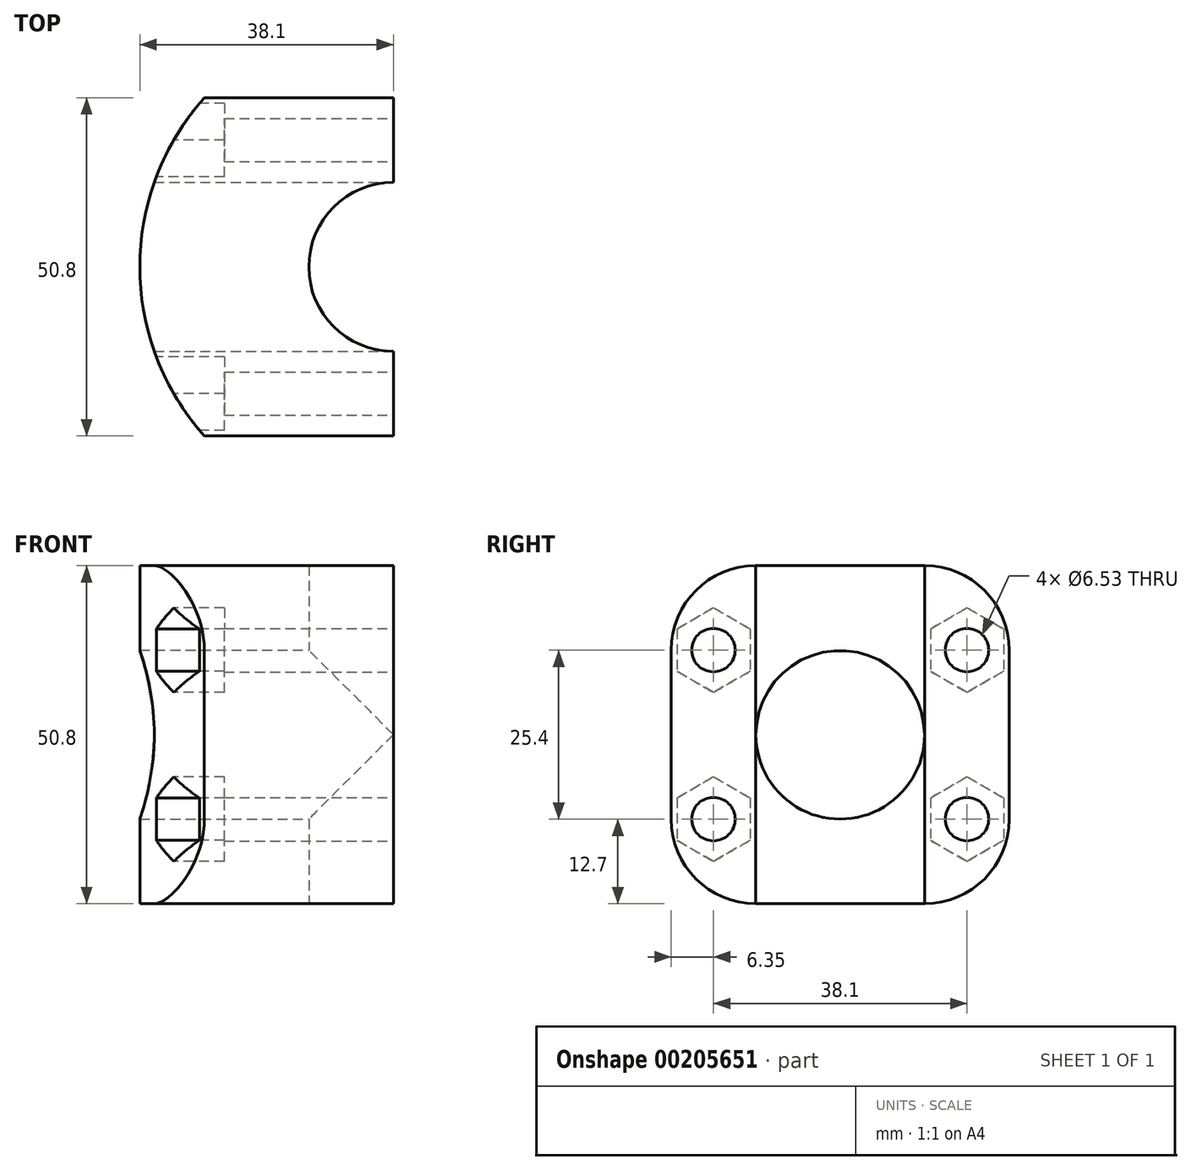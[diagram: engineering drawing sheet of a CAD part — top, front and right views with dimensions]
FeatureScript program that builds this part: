
annotation { "Feature Type Name" : "Feature", "Feature Type Description" : "" }
export const myFeature = defineFeature(function(context is Context, id is Id, definition is map)
    precondition{}
    {
        {
            var Q0;
            Q0=qCreatedBy(makeId("Top.planeOp"),FACE);
            var sketch = newSketch(context, id + "F0", { "sketchPlane" : qUnion([Q0])});
            skLineSegment(sketch, "E0.bottom", {"start": v(-28.4, 50.8) * mm, "end": v(0, 50.8) * mm});
            skLineSegment(sketch, "E0.top", {"start": v(-28.4, 0) * mm, "end": v(0, 0) * mm});
            skLineSegment(sketch, "E0.right", {"start": v(0, 50.8) * mm, "end": v(0, 38.1) * mm});
            skArc(sketch, "E1", {"start": v(0, 38.1) * mm, "mid": v(-12.7, 25.4) * mm, "end": v(0, 12.7) * mm});
            skArc(sketch, "E2", {"start": v(-28.4, 50.8) * mm, "mid": v(-38.1, 25.4) * mm, "end": v(-28.4, 0) * mm});
            skLineSegment(sketch, "E3.trimOffspring", {"start": v(0, 12.7) * mm, "end": v(0, 0) * mm});
            skSolve(sketch);
        }
        {
            var Q0;
            Q0 = qSketchRegion(id + "F0", true);
            extrude(context, id + "F1", {"entities" : qUnion([Q0]), "endBound" : BoundingType.SYMMETRIC, "depth" : 50.8 * mm});
        }
        {
            var Q0;
            Q0=qCreatedBy(makeId("Right.planeOp"),FACE);
            var sketch = newSketch(context, id + "F2", { "sketchPlane" : qUnion([Q0])});
            skPoint(sketch, "E4", {"position": v(44.45, 12.7) * mm});
            skPoint(sketch, "E5", {"position": v(44.45, -12.7) * mm});
            skPoint(sketch, "E6", {"position": v(6.35, -12.7) * mm});
            skPoint(sketch, "E7", {"position": v(6.35, 12.7) * mm});
            skLineSegment(sketch, "E8", {"start": v(50.8, 12.7) * mm, "end": v(0, 12.7) * mm});
            skLineSegment(sketch, "E9", {"start": v(50.8, -12.7) * mm, "end": v(0, -12.7) * mm});
            skLineSegment(sketch, "E10", {"start": v(6.35, 25.4) * mm, "end": v(6.35, -25.4) * mm});
            skLineSegment(sketch, "E11", {"start": v(44.45, 25.4) * mm, "end": v(44.45, -25.4) * mm});
            skLineSegment(sketch, "E12", {"start": v(25.4, 12.7) * mm, "end": v(25.4, -12.7) * mm});
            skLineSegment(sketch, "E13", {"start": v(6.35, 0) * mm, "end": v(44.45, 0) * mm});
            skPoint(sketch, "E14", {"position": v(25.4, 0) * mm});
            skSolve(sketch);
        }
        {
            var Q0;
            Q0=sQuery(id+"F2.wireOp",VERTEX,"E7");
            var Q1;
            Q1=sQuery(id+"F2.wireOp",VERTEX,"E4");
            var Q2;
            Q2=sQuery(id+"F2.wireOp",VERTEX,"E5");
            var Q3;
            Q3=sQuery(id+"F2.wireOp",VERTEX,"E6");
            var Q4;
            Q4=makeQuery(id+"F1.opExtrude","SWEPT_BODY",BODY,{"disambiguationData":[OSD([sQuery(id+"F0.wireOp",EDGE,"E0.bottom"),sQuery(id+"F0.wireOp",EDGE,"E0.top"),sQuery(id+"F0.wireOp",EDGE,"E0.right"),sQuery(id+"F0.wireOp",EDGE,"E1"),sQuery(id+"F0.wireOp",EDGE,"E2"),sQuery(id+"F0.wireOp",EDGE,"E3.trimOffspring")])]});
            hole(context, id + "F3", {"style" : HoleStyle.SIMPLE, "endStyle" : HoleEndStyle.THROUGH, "standardTappedOrClearance" : lookupTablePath({ "standard" : "ANSI", "fit" : "Close", "size" : "1/4", "type" : "Clearance" }), "standardBlindInLast" : lookupTablePath({ "fit" : "Close", "standard" : "ANSI", "size" : "1/4", "type" : "Clearance" }), "holeDiameter" : 6.53 * mm, "locations" : qUnion([Q0, Q1, Q2, Q3]), "scope" : qUnion([Q4]), "isTappedThrough" : true});
        }
        {
            var Q0;
            Q0=makeQuery(id+"F1.opExtrude","CAP_EDGE",EDGE,{"disambiguationData":[OSD([sQuery(id+"F0.wireOp",EDGE,"E2")])],"isStart":false});
            cPoint(context, id + "F4", {"entities" : qUnion([Q0]), "parameter" : 0.5});
        }
        {
            var Q0;
            Q0=qCreatedBy(makeId("Right.planeOp"),FACE);
            var Q1;
            Q1 = qCreatedBy(id + "F4" ,VERTEX);
            cPlane(context, id + "F5", {"entities" : qUnion([Q0, Q1]), "cplaneType" : CPlaneType.PLANE_POINT, "offset" : 25.4 * mm, "width" : 152.4 * mm, "height" : 152.4 * mm});
        }
        {
            var Q0;
            Q0=qCreatedBy(id+"F5.planeOp",FACE);
            var sketch = newSketch(context, id + "F6", { "sketchPlane" : qUnion([Q0])});
            skCircle(sketch, "E15.cCircle", {"center": v(6.35, 12.7) * mm, "radius": 5.5 * mm, "construction": true});
            skLineSegment(sketch, "E15.0", {"start": v(0.85, 9.52) * mm, "end": v(0.85, 15.88) * mm});
            skLineSegment(sketch, "E15.1", {"start": v(0.85, 15.88) * mm, "end": v(6.35, 19.05) * mm});
            skLineSegment(sketch, "E15.2", {"start": v(6.35, 19.05) * mm, "end": v(11.85, 15.88) * mm});
            skLineSegment(sketch, "E15.3", {"start": v(11.85, 15.88) * mm, "end": v(11.85, 9.53) * mm});
            skLineSegment(sketch, "E15.4", {"start": v(11.85, 9.53) * mm, "end": v(6.35, 6.35) * mm});
            skLineSegment(sketch, "E15.5", {"start": v(6.35, 6.35) * mm, "end": v(0.85, 9.52) * mm});
            skPoint(sketch, "E15.0.midPoint", {"position": v(0.85, 12.7) * mm});
            skCircle(sketch, "E16.cCircle", {"center": v(44.45, 12.7) * mm, "radius": 5.5 * mm, "construction": true});
            skLineSegment(sketch, "E16.0", {"start": v(38.95, 9.53) * mm, "end": v(38.95, 15.87) * mm});
            skLineSegment(sketch, "E16.1", {"start": v(38.95, 15.87) * mm, "end": v(44.45, 19.05) * mm});
            skLineSegment(sketch, "E16.2", {"start": v(44.45, 19.05) * mm, "end": v(49.95, 15.87) * mm});
            skLineSegment(sketch, "E16.3", {"start": v(49.95, 15.88) * mm, "end": v(49.95, 9.52) * mm});
            skLineSegment(sketch, "E16.4", {"start": v(49.95, 9.53) * mm, "end": v(44.45, 6.35) * mm});
            skLineSegment(sketch, "E16.5", {"start": v(44.45, 6.35) * mm, "end": v(38.95, 9.53) * mm});
            skPoint(sketch, "E16.0.midPoint", {"position": v(38.95, 12.7) * mm});
            skCircle(sketch, "E17.cCircle", {"center": v(44.45, -12.7) * mm, "radius": 5.5 * mm, "construction": true});
            skLineSegment(sketch, "E17.0", {"start": v(38.95, -9.52) * mm, "end": v(44.45, -6.35) * mm});
            skLineSegment(sketch, "E17.1", {"start": v(44.45, -6.35) * mm, "end": v(49.95, -9.53) * mm});
            skLineSegment(sketch, "E17.2", {"start": v(49.95, -9.52) * mm, "end": v(49.95, -15.87) * mm});
            skLineSegment(sketch, "E17.3", {"start": v(49.95, -15.87) * mm, "end": v(44.45, -19.05) * mm});
            skLineSegment(sketch, "E17.4", {"start": v(44.45, -19.05) * mm, "end": v(38.95, -15.87) * mm});
            skLineSegment(sketch, "E17.5", {"start": v(38.95, -15.87) * mm, "end": v(38.95, -9.53) * mm});
            skPoint(sketch, "E17.0.midPoint", {"position": v(41.7, -7.94) * mm});
            skCircle(sketch, "E18.cCircle", {"center": v(6.35, -12.7) * mm, "radius": 5.5 * mm, "construction": true});
            skLineSegment(sketch, "E18.0", {"start": v(0.85, -9.53) * mm, "end": v(6.35, -6.35) * mm});
            skLineSegment(sketch, "E18.1", {"start": v(6.35, -6.35) * mm, "end": v(11.85, -9.52) * mm});
            skLineSegment(sketch, "E18.2", {"start": v(11.85, -9.53) * mm, "end": v(11.85, -15.88) * mm});
            skLineSegment(sketch, "E18.3", {"start": v(11.85, -15.88) * mm, "end": v(6.35, -19.05) * mm});
            skLineSegment(sketch, "E18.4", {"start": v(6.35, -19.05) * mm, "end": v(0.85, -15.88) * mm});
            skLineSegment(sketch, "E18.5", {"start": v(0.85, -15.88) * mm, "end": v(0.85, -9.53) * mm});
            skPoint(sketch, "E18.0.midPoint", {"position": v(3.6, -7.94) * mm});
            skSolve(sketch);
        }
        {
            var Q0;
            Q0 = qSketchRegion(id + "F6", true);
            extrude(context, id + "F7", {"entities" : qUnion([Q0]), "operationType" : NewBodyOperationType.REMOVE, "depth" : 12.7 * mm});
        }
        {
            var Q0;
            Q0=makeQuery(id+"F1.opExtrude","CAP_EDGE",EDGE,{"disambiguationData":[OSD([sQuery(id+"F0.wireOp",EDGE,"E0.top")])],"isStart":false});
            var Q1;
            Q1=makeQuery(id+"F1.opExtrude","CAP_EDGE",EDGE,{"disambiguationData":[OSD([sQuery(id+"F0.wireOp",EDGE,"E0.bottom")])],"isStart":false});
            var Q2;
            Q2=makeQuery(id+"F1.opExtrude","CAP_EDGE",EDGE,{"disambiguationData":[OSD([sQuery(id+"F0.wireOp",EDGE,"E0.top")])],"isStart":true});
            var Q3;
            Q3=makeQuery(id+"F1.opExtrude","CAP_EDGE",EDGE,{"disambiguationData":[OSD([sQuery(id+"F0.wireOp",EDGE,"E0.bottom")])],"isStart":true});
            fillet(context, id + "F8", {"entities" : qUnion([Q0, Q1, Q2, Q3]), "radius" : 12.7 * mm, "tangentPropagation" : true, "allowEdgeOverflow" : false});
        }
        {
            var Q0;
            Q0=sQuery(id+"F2.wireOp",VERTEX,"E14");
            var Q1;
            Q1=makeQuery(id+"F1.opExtrude","SWEPT_BODY",BODY,{"disambiguationData":[OSD([sQuery(id+"F0.wireOp",EDGE,"E0.bottom"),sQuery(id+"F0.wireOp",EDGE,"E0.top"),sQuery(id+"F0.wireOp",EDGE,"E0.right"),sQuery(id+"F0.wireOp",EDGE,"E1"),sQuery(id+"F0.wireOp",EDGE,"E2"),sQuery(id+"F0.wireOp",EDGE,"E3.trimOffspring")])]});
            hole(context, id + "F9", {"style" : HoleStyle.SIMPLE, "endStyle" : HoleEndStyle.THROUGH, "holeDiameter" : 25.4 * mm, "locations" : qUnion([Q0]), "scope" : qUnion([Q1]), "isTappedThrough" : true});
        }
    });
